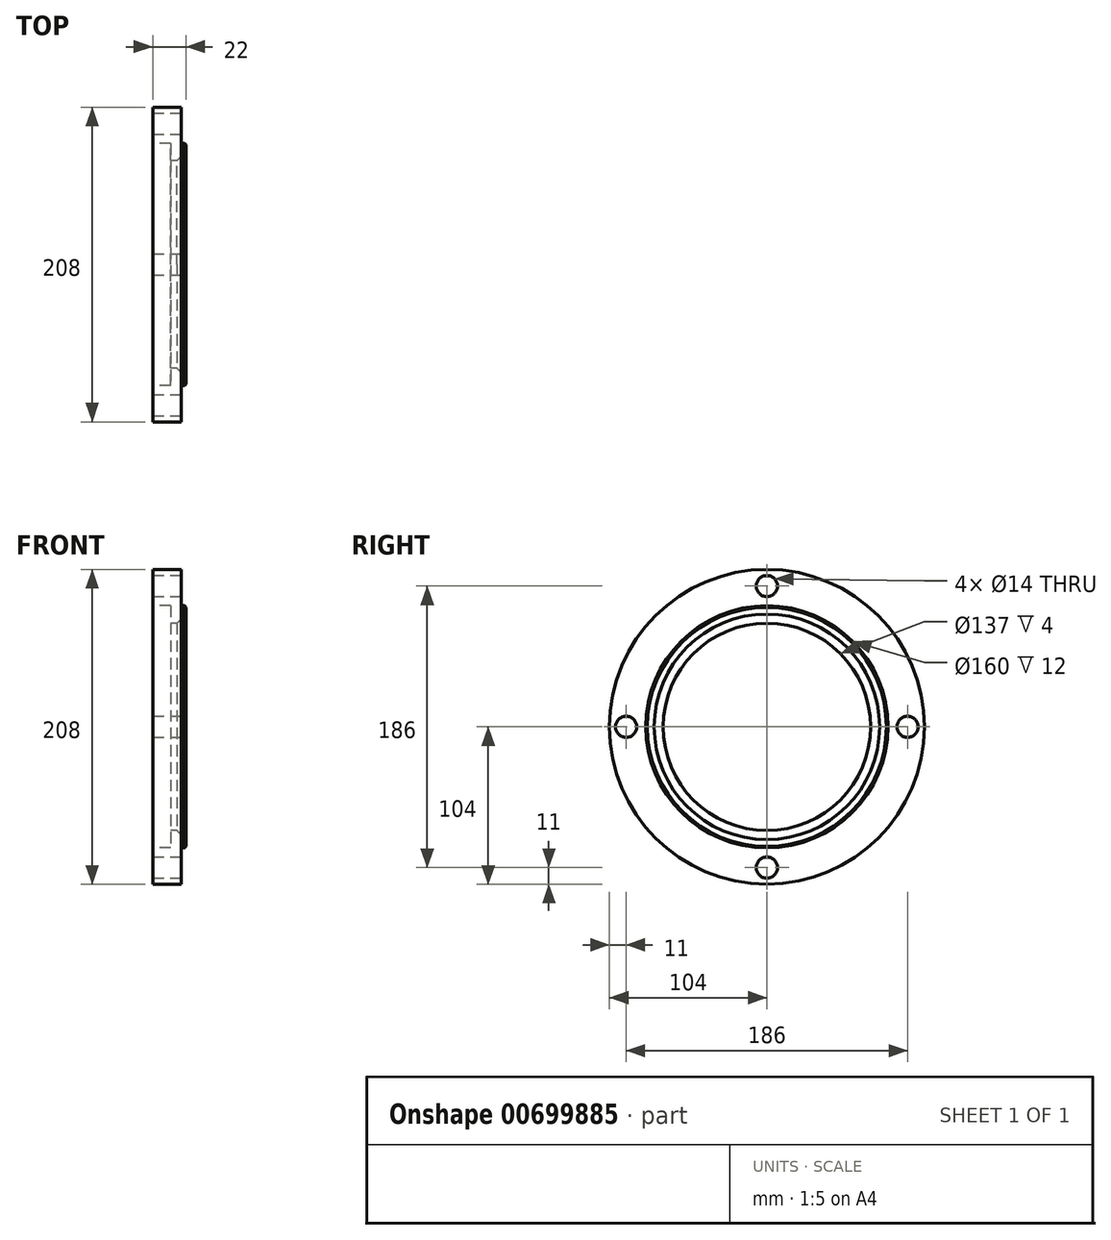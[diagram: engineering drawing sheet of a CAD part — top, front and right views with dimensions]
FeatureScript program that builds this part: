
annotation { "Feature Type Name" : "Feature", "Feature Type Description" : "" }
export const myFeature = defineFeature(function(context is Context, id is Id, definition is map)
    precondition{}
    {
        {
            var Q0;
            Q0=qCreatedBy(makeId("Right.planeOp"),FACE);
            var sketch = newSketch(context, id + "F0", { "sketchPlane" : qUnion([Q0])});
            skCircle(sketch, "E0", {"center": v(0, 0) * mm, "radius": 104 * mm});
            skCircle(sketch, "E1", {"center": v(0, 0) * mm, "radius": 68.5 * mm});
            skSolve(sketch);
        }
        {
            var Q0;
            Q0 = qSketchRegion(id + "F0", true);
            extrude(context, id + "F1", {"entities" : qUnion([Q0]), "endBound" : BoundingType.SYMMETRIC, "depth" : 19 * mm, "offsetDistance" : 25 * mm});
        }
        {
            var Q0;
            Q0=makeQuery(id+"F1.opExtrude","CAP_FACE",FACE,{"disambiguationData":[OSD([sQuery(id+"F0.wireOp",EDGE,"E0"),sQuery(id+"F0.wireOp",EDGE,"E1")])],"isStart":false});
            var sketch = newSketch(context, id + "F2", { "sketchPlane" : qUnion([Q0])});
            skCircle(sketch, "E2.0", {"center": v(0, 0) * mm, "radius": 104 * mm, "construction": true});
            skCircle(sketch, "E3", {"center": v(0, 0) * mm, "radius": 93 * mm, "construction": true});
            skLineSegment(sketch, "E4", {"start": v(0, 0) * mm, "end": v(0, 93) * mm, "construction": true});
            skPoint(sketch, "E5", {"position": v(0, 93) * mm});
            skPoint(sketch, "E6.1.0", {"position": v(-93, 0) * mm});
            skPoint(sketch, "E6.2.0", {"position": v(0, -93) * mm});
            skPoint(sketch, "E6.3.0", {"position": v(93, 0) * mm});
            skSolve(sketch);
        }
        {
            var Q0;
            Q0=sQuery(id+"F2.wireOp",VERTEX,"E5");
            var Q1;
            Q1=sQuery(id+"F2.wireOp",VERTEX,"E6.3.0");
            var Q2;
            Q2=sQuery(id+"F2.wireOp",VERTEX,"E6.2.0");
            var Q3;
            Q3=sQuery(id+"F2.wireOp",VERTEX,"E6.1.0");
            var Q4;
            Q4=makeQuery(id+"F1.opExtrude","SWEPT_BODY",BODY,{"disambiguationData":[OSD([sQuery(id+"F0.wireOp",EDGE,"E0"),sQuery(id+"F0.wireOp",EDGE,"E1")])]});
            hole(context, id + "F3", {"style" : HoleStyle.SIMPLE, "endStyle" : HoleEndStyle.THROUGH, "standardTappedOrClearance" : lookupTablePath({ "standard" : "ISO", "size" : "14", "type" : "Drilled" }), "standardBlindInLast" : lookupTablePath({ "standard" : "ISO", "size" : "14", "type" : "Drilled" }), "holeDiameter" : 14 * mm, "majorDiameter" : 5 * mm, "isTappedThrough" : true, "tappedDepth" : 12 * mm, "tapClearance" : 3, "locations" : qUnion([Q0, Q1, Q2, Q3]), "scope" : qUnion([Q4])});
        }
        {
            var Q0;
            Q0=makeQuery(id+"F1.opExtrude","CAP_FACE",FACE,{"disambiguationData":[OSD([sQuery(id+"F0.wireOp",EDGE,"E0"),sQuery(id+"F0.wireOp",EDGE,"E1")])],"isStart":true});
            var sketch = newSketch(context, id + "F4", { "sketchPlane" : qUnion([Q0])});
            skCircle(sketch, "E7.0", {"center": v(0, 0) * mm, "radius": 68.5 * mm, "construction": true});
            skCircle(sketch, "E8", {"center": v(0, 0) * mm, "radius": 80 * mm});
            skSolve(sketch);
        }
        {
            var Q0;
            Q0 = qSketchRegion(id + "F4", true);
            extrude(context, id + "F5", {"entities" : qUnion([Q0]), "operationType" : NewBodyOperationType.REMOVE, "oppositeDirection" : true, "depth" : 12 * mm, "offsetDistance" : 25 * mm});
        }
        {
            var Q0;
            Q0=makeQuery(id+"F1.opExtrude","CAP_FACE",FACE,{"disambiguationData":[OSD([sQuery(id+"F0.wireOp",EDGE,"E0"),sQuery(id+"F0.wireOp",EDGE,"E1")])],"isStart":false});
            var sketch = newSketch(context, id + "F6", { "sketchPlane" : qUnion([Q0])});
            skCircle(sketch, "E9.0", {"center": v(0, 0) * mm, "radius": 68.5 * mm});
            skCircle(sketch, "E10", {"center": v(0, 0) * mm, "radius": 80 * mm});
            skSolve(sketch);
        }
        {
            var Q0;
            Q0 = qSketchRegion(id + "F6", true);
            extrude(context, id + "F7", {"entities" : qUnion([Q0]), "operationType" : NewBodyOperationType.ADD, "depth" : 3 * mm, "offsetDistance" : 25 * mm});
        }
        {
            var Q0;
            Q0=makeQuery(id+"F7.opExtrude","CAP_EDGE",EDGE,{"disambiguationData":[OSD([sQuery(id+"F6.wireOp",EDGE,"E10")])],"isStart":false});
            chamfer(context, id + "F8", {"entities" : qUnion([Q0]), "width" : 1 * mm, "tangentPropagation" : true});
        }
        {
            var Q0;
            Q0=makeQuery(id+"F7.opExtrude","CAP_EDGE",EDGE,{"disambiguationData":[OSD([sQuery(id+"F6.wireOp",EDGE,"E9.0")])],"isStart":false});
            chamfer(context, id + "F9", {"entities" : qUnion([Q0]), "width" : 6 * mm, "tangentPropagation" : true});
        }
    });
